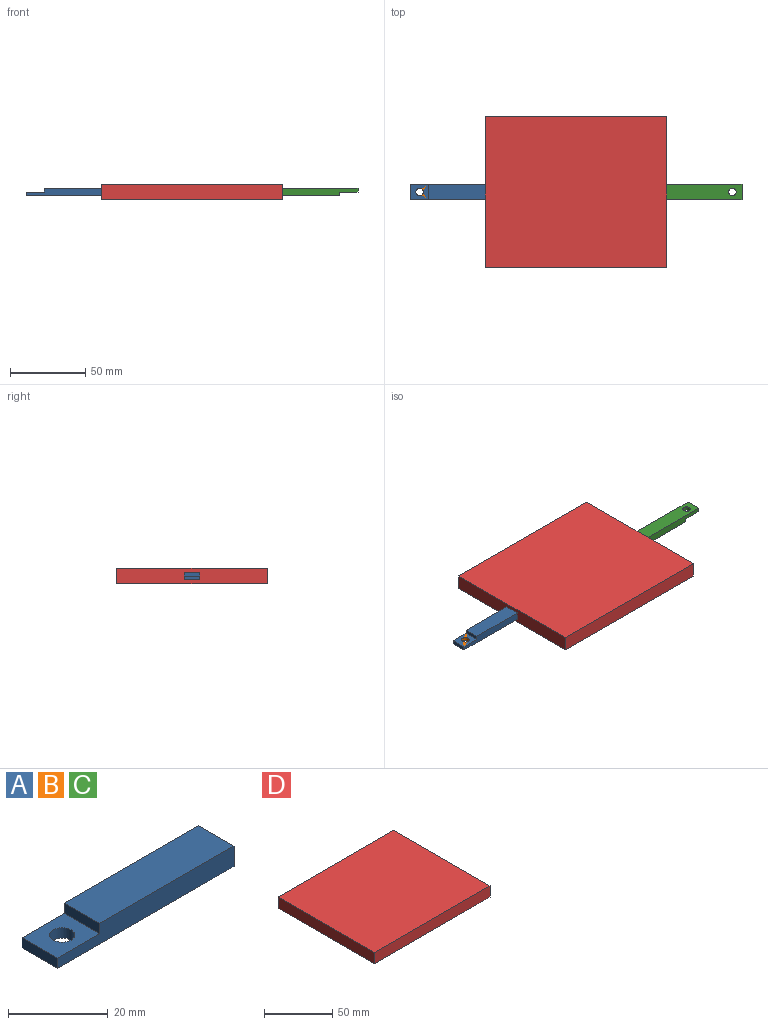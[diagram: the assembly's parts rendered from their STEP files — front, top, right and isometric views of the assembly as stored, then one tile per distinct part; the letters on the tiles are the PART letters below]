
ASSEMBLY  parts=4 mates=2
PART A: 9 faces, bbox 50x10x5 mm
  f0: plane 50x5mm, normal (0,1,0), area 220mm2, adj f1,f3,f4,f5,f7,f8
  f1: plane 10x2.5mm, normal (-1,0,0), area 25mm2, adj f0,f2,f5,f8
  f2: plane 50x5mm, normal (0,-1,0), area 220mm2, adj f1,f3,f4,f5,f7,f8
  f3: plane 10x5mm, normal (1,0,0), area 50mm2, adj f0,f2,f4,f5
  f4: plane 38x10mm, normal (0,0,1), area 380mm2, adj f0,f2,f3,f7
  f5: plane 50x10mm, normal (0,0,-1), area 480.4mm2, adj f0,f1,f2,f3,f6
  f6: cylinder r=2.5mm len=5mm, axis (0,0,1), area 39.3mm2, adj f5,f8
  f7: plane 10x2.5mm, normal (-1,0,0), area 25mm2, adj f0,f2,f4,f8
  f8: plane 12x10mm, normal (0,0,1), area 100.4mm2, adj f0,f1,f2,f6,f7
PART B: same geometry as A
PART C: same geometry as A
PART D: 6 faces, bbox 120x100x10 mm
  f0: plane 120x10mm, normal (0,1,0), area 1200mm2, adj f1,f3,f4,f5
  f1: plane 100x10mm, normal (-1,0,0), area 1000mm2, adj f0,f2,f4,f5
  f2: plane 120x10mm, normal (0,-1,0), area 1200mm2, adj f1,f3,f4,f5
  f3: plane 100x10mm, normal (1,0,0), area 1000mm2, adj f0,f2,f4,f5
  f4: plane 120x100mm, normal (0,0,1), area 12000mm2, adj f0,f1,f2,f3
  f5: plane 120x100mm, normal (0,0,-1), area 12000mm2, adj f0,f1,f2,f3
PLACE A t=(31.18,-11.91,32.31)mm
PLACE B t=(31.18,-11.91,32.31)mm
PLACE C rot(axis=(0,1,0),180deg) t=(15.28,-11.91,37.31)mm
PLACE D t=(20.81,-13.64,29.81)mm
MATE fastened D.f1 <-> A.f3  axis (-1,0,0) through (-36.77,-12.45,34.81)mm
MATE fastened C.f3 <-> D.f3  axis (-1,0,0) through (83.23,-12.45,34.81)mm
